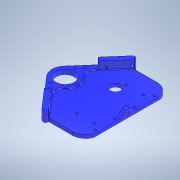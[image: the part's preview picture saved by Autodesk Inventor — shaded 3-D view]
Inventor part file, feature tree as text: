
AUTODESK INVENTOR PART (.ipt)
format: ipt  version: 2022 (Build 260153000, 153)  size: 404,480 bytes
history: native  units: in
note: dims shown in document units (in); Inventor stores cm internally (conversion verified against a paired STEP export)
features: reference x22, sketch x11, extrude x9, other x7, hole x5, projected_geometry x4, fillet x3, mirror x1, chamfer x1
ambient origin geometry x8: Origin, YZ Plane, XZ Plane, XY Plane, X Axis, Y Axis, Z Axis, Center Point
bodies: Solid3 (feature_tree)
feature tree (63):
  extrude  "Extrusion13"  Depth=2.1654in
  extrude  "Extrusion14"  Depth=0.4433in TaperAngle=0.0deg
  mirror  "Mirror4"
  extrude  "Extrusion25"  Depth=0.1969in TaperAngle=0.0deg
  extrude  "Extrusion26"  Depth=0.7874in
  extrude  "Extrusion28"  Depth=0.1969in
  extrude  "Extrusion35"  Depth=0.0787in
  extrude  "Extrusion38"  Depth=1.1024in
  extrude  "Extrusion39"  Depth=0.3937in TaperAngle=0.0deg
  hole  "Hole5"  [1 undecoded]
  fillet  "Fillet3"  Radius=0.4724in
  hole  "Hole6"  [1 undecoded]
  fillet  "Fillet4"  Radius=1.7717in
  chamfer  "Chamfer3"  Distance=1.8504in
  hole  "Hole7"  [1 undecoded]
  hole  "Hole8"  [1 undecoded]
  extrude  "Extrusion40"  Depth=0.0394in
  hole  "Hole9"  [1 undecoded]
  fillet  "Fillet5"  Radius=0.2913in
  sketch  "Sketch14"  dims[d94=0.9646in d95=2.1654in]
  sketch  "Sketch15"  dims[d96=1.7717in d97=0.4433in d98=0.0in]
  projected_geometry  "Projected Loop7"
  sketch  "Sketch26"  dims[d99=2.5561in d100=0.1969in d101=0.0in]
  sketch  "Sketch27"  dims[d137=0.7874in d138=1.5748in]
  sketch  "Sketch29"  dims[d139=0.1969in d140=0.0in d141=1.1024in]
  sketch  "Sketch37"  dims[d143=0.0787in d144=0.0in d145=0.5906in]
  projected_geometry  "Projected Loop19"
  sketch  "Sketch40"  dims[d146=1.1024in d149=1.1024in]
  sketch  "Sketch41"  dims[d151=0.6299in d152=0.3937in d153=0.0in]
  projected_geometry  "Projected Loop20"
  sketch  "Sketch42"  dims[d185=0.0in d186=0.0in d198=0.4724in d199=0.4724in]
  reference  "Reference1"
  reference  "Reference2"
  reference  "Reference3"
  reference  "Reference4"
  reference  "Reference5"
  reference  "Reference6"
  reference  "Reference7"
  reference  "Reference8"
  reference  "Reference9"
  reference  "Reference10"
  reference  "Reference11"
  reference  "Reference12"
  reference  "Reference13"
  reference  "Reference14"
  reference  "Reference15"
  reference  "Reference16"
  reference  "Reference17"
  reference  "Reference18"
  reference  "Reference19"
  sketch  "Sketch45"  dims[d200=0.0in d201=0.0in d202=1.5354in d203=1.7717in]
  reference  "Reference20"
  reference  "Reference21"
  sketch  "Sketch46"  dims[d204=1.8504in d205=1.8504in d206=0.3937in d207=0.0in d208=0.1575in d209=0.2362in d210=0.248in d211=0.0787in d212=90.0deg d213=0.315in d214=0.8108in d215=0.1575in d216=0.1575in d217=0.315in d218=0.1575in d219=0.0787in d220=90.0deg d221=0.2756in d222=0.8108in d223=0.0394in d224=0.0394in d225=0.0787in d226=45.0deg d227=0.1575in d228=0.2362in d229=0.248in d230=0.0787in d231=90.0deg d232=0.315in d233=0.8108in d234=0.1575in d235=0.2362in d236=0.1575in d237=0.0787in d238=90.0deg d239=0.315in d240=0.8108in d241=0.2913in d242=0.315in d243=135.0deg d244=0.1969in d245=0.0in d246=0.1575in d247=0.2362in d248=0.1575in d249=0.0787in d250=90.0deg d251=0.315in d252=0.0in d253=0.7874in d93=0.1575in d107=0.0197in d108=0.0344in d109=0.0197in d110=0.0344in d154=0.0197in d155=0.0344in]
  projected_geometry  "Projected Loop21"
  reference  "Reference22"
  parser-record x1  (decoder bookkeeping rows leaked as tree rows — omitted from the tree; the rows remain in map.json)
  other  "Main Body.iam"
  other  "ESC Mount:1"
  other  "ESC Mount:2"
  other  "Base Plate:1"
  other  "Front Armor:1"
  other  "Front Armor:2"
note: 5 required parameter values undecoded (feature->parameter linkage not recoverable at this tier; creation-order binding heuristic only, values carry confidence <= 0.55)
note: 1 file-system path scrubbed to <path> (originals preserved in map.json)
